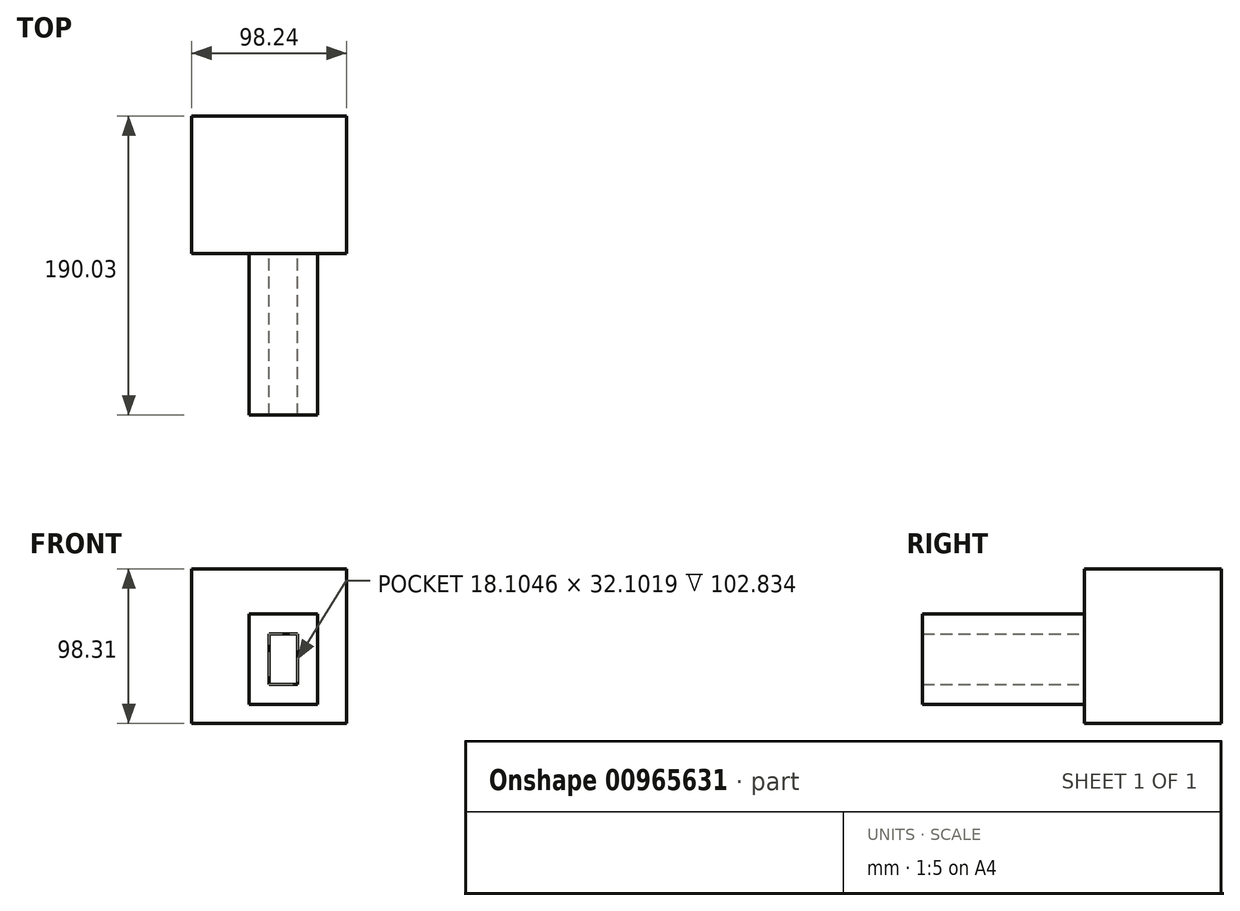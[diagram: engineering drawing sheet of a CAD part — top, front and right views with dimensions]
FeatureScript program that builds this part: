
annotation { "Feature Type Name" : "Feature", "Feature Type Description" : "" }
export const myFeature = defineFeature(function(context is Context, id is Id, definition is map)
    precondition{}
    {
        {
            var Q0;
            Q0=qCreatedBy(makeId("Top.planeOp"),FACE);
            var sketch = newSketch(context, id + "F0", { "sketchPlane" : qUnion([Q0])});
            skLineSegment(sketch, "E0.bottom", {"start": v(49.12, 43.6) * mm, "end": v(-49.12, 43.6) * mm});
            skLineSegment(sketch, "E0.top", {"start": v(49.12, -43.6) * mm, "end": v(-49.12, -43.6) * mm});
            skLineSegment(sketch, "E0.left", {"start": v(49.12, 43.6) * mm, "end": v(49.12, -43.6) * mm});
            skLineSegment(sketch, "E0.right", {"start": v(-49.12, 43.6) * mm, "end": v(-49.12, -43.6) * mm});
            skPoint(sketch, "E0.middle", {"position": v(0, 0) * mm});
            skSolve(sketch);
        }
        {
            var Q0;
            Q0 = qSketchRegion(id + "F0", true);
            extrude(context, id + "F1", {"entities" : qUnion([Q0]), "depth" : 98.3 * mm, "offsetDistance" : 25.4 * mm});
        }
        {
            var Q0;
            Q0=makeQuery(id+"F1.opExtrude","SWEPT_FACE",FACE,{"disambiguationData":[OSD([sQuery(id+"F0.wireOp",EDGE,"E0.top")])]});
            var sketch = newSketch(context, id + "F2", { "sketchPlane" : qUnion([Q0])});
            skLineSegment(sketch, "E1.bottom", {"start": v(18.1, 24.69) * mm, "end": v(0, 24.69) * mm});
            skLineSegment(sketch, "E1.top", {"start": v(18.1, 56.79) * mm, "end": v(0, 56.79) * mm});
            skLineSegment(sketch, "E1.left", {"start": v(18.1, 24.69) * mm, "end": v(18.1, 56.79) * mm});
            skLineSegment(sketch, "E1.right", {"start": v(0, 24.69) * mm, "end": v(0, 56.79) * mm});
            skLineSegment(sketch, "E2.0", {"start": v(30.8, 11.99) * mm, "end": v(30.8, 69.49) * mm});
            skLineSegment(sketch, "E2.1", {"start": v(30.8, 11.99) * mm, "end": v(-12.7, 11.99) * mm});
            skLineSegment(sketch, "E2.2", {"start": v(-12.7, 11.99) * mm, "end": v(-12.7, 69.49) * mm});
            skLineSegment(sketch, "E2.3", {"start": v(30.8, 69.49) * mm, "end": v(-12.7, 69.49) * mm});
            skSolve(sketch);
        }
        {
            var Q0;
            Q0=makeQuery(id+"F2.imprint","IMPRINT",FACE,{"disambiguationData":[TD([[makeQuery(id+"F2.imprint","IMPRINT",EDGE,{"derivedFrom":sQuery(id+"F2.wireOp",EDGE,"E1.bottom")}),1.0]])]});
            extrude(context, id + "F3", {"entities" : qUnion([Q0]), "operationType" : NewBodyOperationType.ADD, "depth" : 102.83 * mm, "offsetDistance" : 25.4 * mm});
        }
    });
